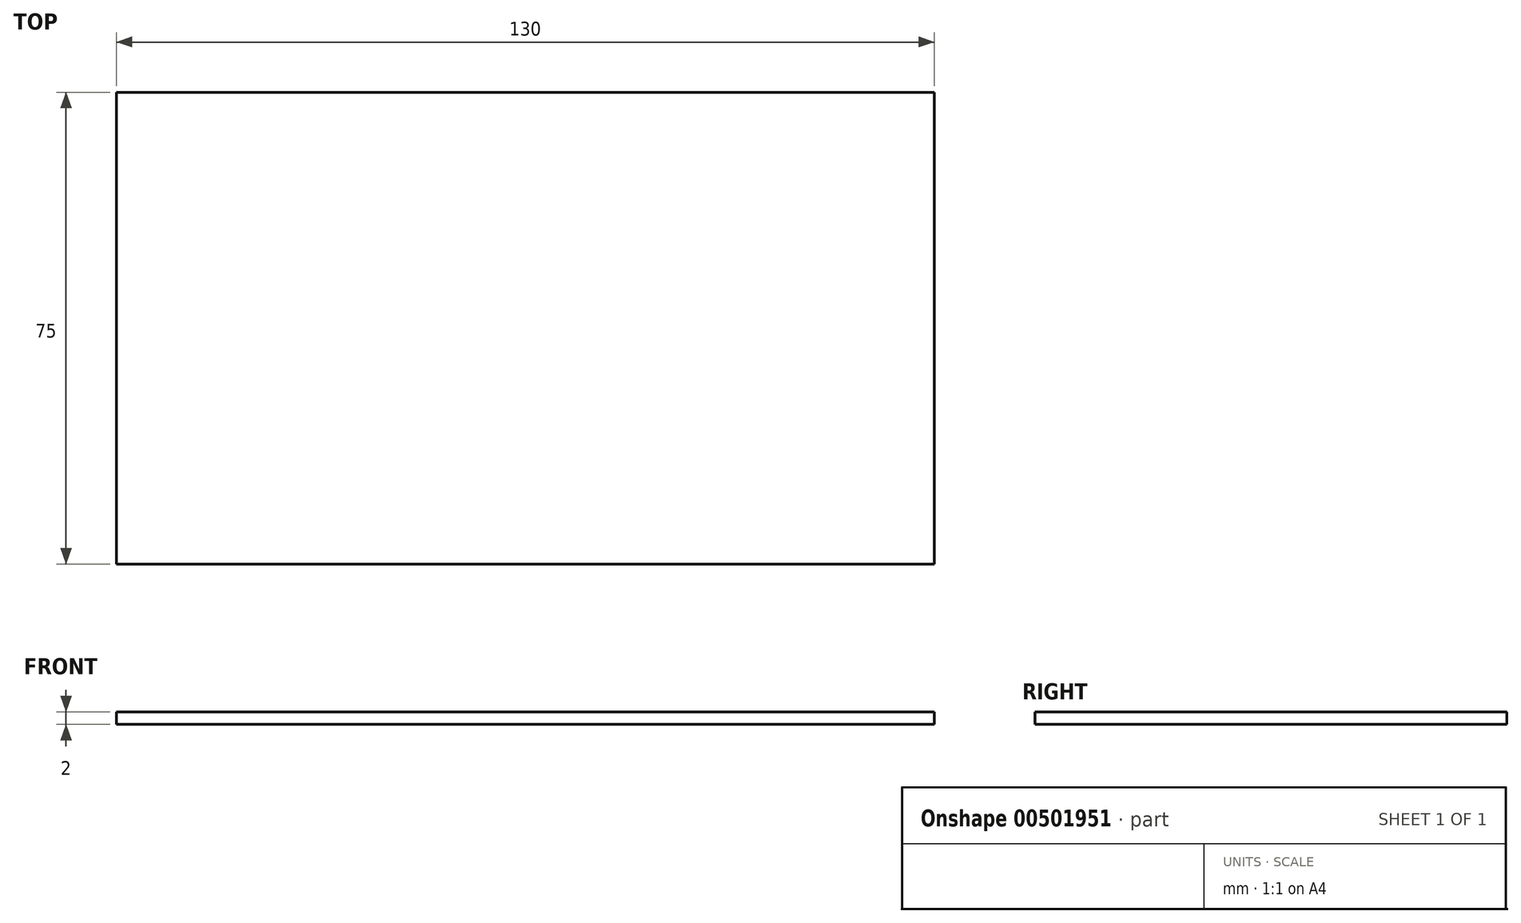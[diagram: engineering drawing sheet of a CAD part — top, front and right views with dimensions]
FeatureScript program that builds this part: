
annotation { "Feature Type Name" : "Feature", "Feature Type Description" : "" }
export const myFeature = defineFeature(function(context is Context, id is Id, definition is map)
    precondition{}
    {
        {
            var Q0;
            Q0=qCreatedBy(makeId("Top.planeOp"),FACE);
            var sketch = newSketch(context, id + "F0", { "sketchPlane" : qUnion([Q0])});
            skLineSegment(sketch, "E0.bottom", {"start": v(65, -37.5) * mm, "end": v(-65, -37.5) * mm});
            skLineSegment(sketch, "E0.top", {"start": v(65, 37.5) * mm, "end": v(-65, 37.5) * mm});
            skLineSegment(sketch, "E0.left", {"start": v(65, -37.5) * mm, "end": v(65, 37.5) * mm});
            skLineSegment(sketch, "E0.right", {"start": v(-65, -37.5) * mm, "end": v(-65, 37.5) * mm});
            skPoint(sketch, "E0.middle", {"position": v(0, 0) * mm});
            skSolve(sketch);
        }
        {
            var Q0;
            Q0=makeQuery(id+"F0.imprint","IMPRINT",FACE,{"disambiguationData":[TD([[makeQuery(id+"F0.imprint","IMPRINT",EDGE,{"derivedFrom":sQuery(id+"F0.wireOp",EDGE,"E0.bottom")}),-1.0]])]});
            extrude(context, id + "F1", {"entities" : qUnion([Q0]), "depth" : 2 * mm, "symmetric" : true});
        }
    });
